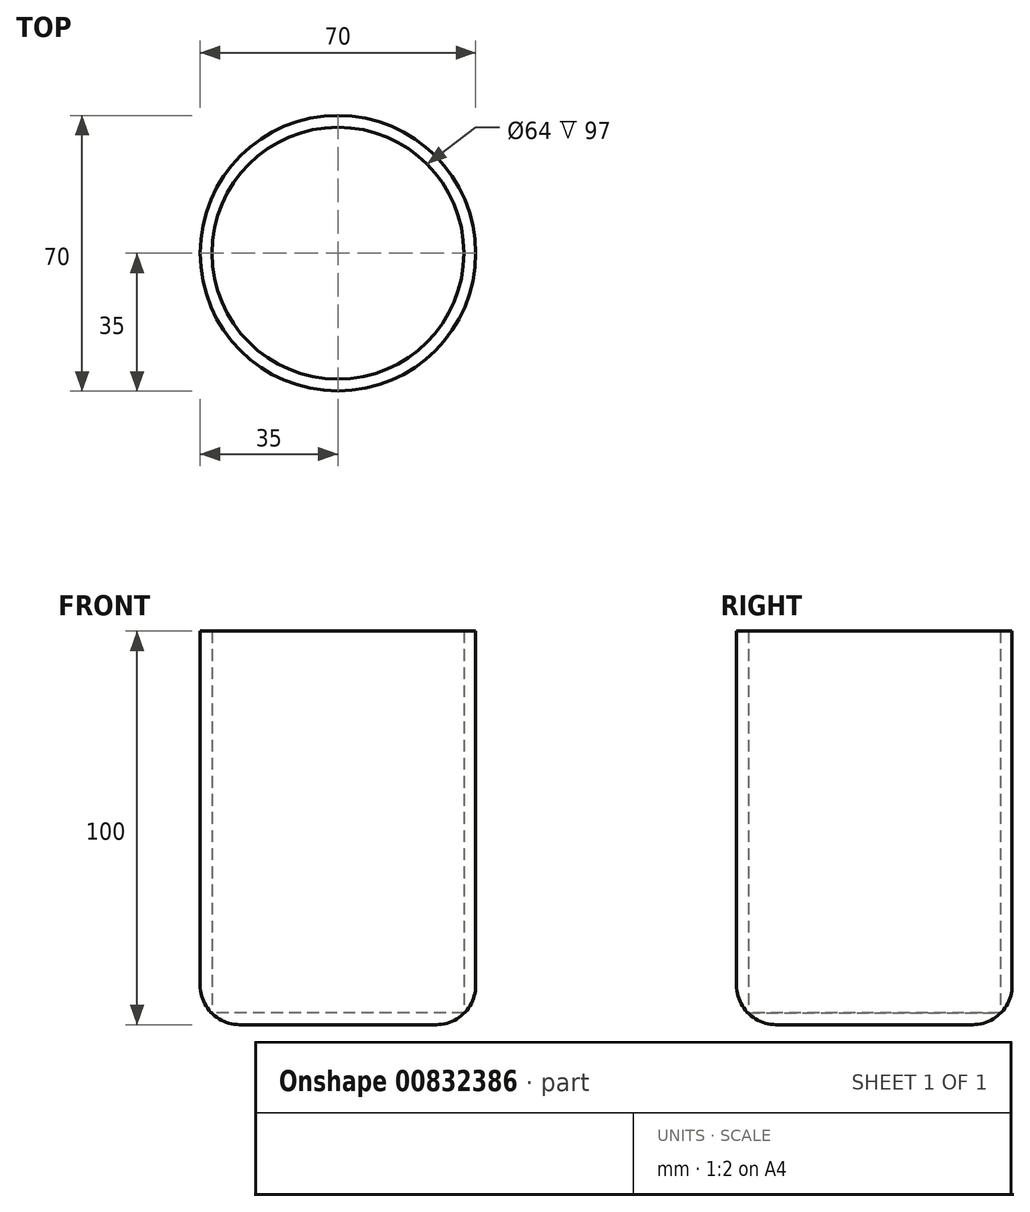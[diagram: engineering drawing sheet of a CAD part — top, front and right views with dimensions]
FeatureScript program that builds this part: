
annotation { "Feature Type Name" : "Feature", "Feature Type Description" : "" }
export const myFeature = defineFeature(function(context is Context, id is Id, definition is map)
    precondition{}
    {
        {
            var Q0;
            Q0=qCreatedBy(makeId("Top.planeOp"),FACE);
            var sketch = newSketch(context, id + "F0", { "sketchPlane" : qUnion([Q0])});
            skCircle(sketch, "E0", {"center": v(0, 0) * mm, "radius": 35 * mm});
            skSolve(sketch);
        }
        {
            var Q0;
            Q0 = qSketchRegion(id + "F0", true);
            extrude(context, id + "F1", {"entities" : qUnion([Q0]), "depth" : 100 * mm, "offsetDistance" : 25 * mm});
        }
        {
            var Q0;
            Q0=makeQuery(id+"F1.opExtrude","CAP_FACE",FACE,{"disambiguationData":[OSD([sQuery(id+"F0.wireOp",EDGE,"E0")])],"isStart":false});
            shell(context, id + "F2", {"entities" : qUnion([Q0]), "thickness" : 3 * mm});
        }
        {
            var Q0;
            Q0=makeQuery(id+"F1.opExtrude","CAP_FACE",FACE,{"disambiguationData":[OSD([sQuery(id+"F0.wireOp",EDGE,"E0")])],"isStart":true});
            fillet(context, id + "F3", {"entities" : qUnion([Q0]), "radius" : 10 * mm, "tangentPropagation" : true, "allowEdgeOverflow" : false});
        }
    });
